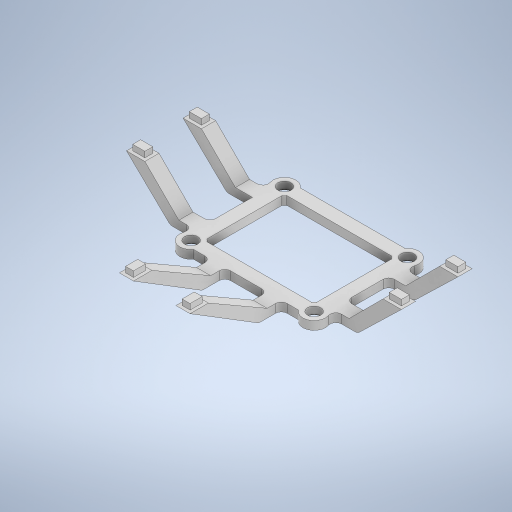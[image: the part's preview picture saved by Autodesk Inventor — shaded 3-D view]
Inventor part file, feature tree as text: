
AUTODESK INVENTOR PART (.ipt)
format: ipt  version: 2024.2 (Build 282272000, 272)  size: 465,920 bytes
history: native  units: mm
features: extrude x5, mirror x5, sketch x5, plane x4, fillet x2, chamfer x1
ambient origin geometry x8: Origin, YZ Plane, XZ Plane, XY Plane, X Axis, Y Axis, Z Axis, Center Point
bodies: Solid1 (feature_tree)
feature tree (22):
  extrude  "Extrusion1"  Depth=8.0mm
  chamfer  "Chamfer1"  Distance=4.7mm
  plane  "Work Plane2"
  extrude  "Extrusion2"  Depth=8.0mm
  plane  "Work Plane4"
  plane  "Work Plane5"
  mirror  "Mirror1"
  mirror  "Mirror2"
  plane  "Work Plane6"
  extrude  "Extrusion5"  Depth=4.0mm
  mirror  "Mirror5"
  extrude  "Extrusion4"  Depth=4.0mm
  mirror  "Mirror3"
  mirror  "Mirror4"
  extrude  "Extrusion6"  Depth=4.0mm
  fillet  "Fillet1"  Radius=4.0mm
  fillet  "Fillet2"  Radius=4.0mm
  sketch  "Sketch1"  dims[d0=4.7mm d1=8.0mm]
  sketch  "Sketch2"  dims[d2=4.7mm]
  sketch  "Sketch5"  dims[d3=8.0mm]
  sketch  "Sketch7"  dims[d4=4.7mm]
  sketch  "Sketch8"  dims[d5=8.0mm d6=4.7mm d7=8.0mm d8=4.0mm d9=4.0mm d10=4.0mm d11=4.0mm d12=4.0mm d13=4.0mm d14=4.0mm d15=4.0mm d16=33.0mm d17=4.7mm d18=4.7mm d19=4.7mm d20=4.7mm d21=2.35mm d22=2.35mm d23=2.35mm d24=2.35mm d25=43.5mm d26=3.0mm d27=0.0mm d28=0.5mm d29=2.0mm d30=45.0deg d32=4.0mm d41=5.0mm d42=0.0mm d47=21.75mm d48=16.5mm d49=6.5mm d61=9.0mm d62=4.3mm d63=2.8mm d64=1.1mm d65=1.1mm d66=2.0mm d67=0.0mm d71=9.25mm d72=8.0mm d73=6.5mm d76=5.0mm d77=0.0mm d78=2.8mm d79=4.3mm d80=2.8mm d81=4.3mm d82=1.1mm d83=1.1mm d84=1.1mm d85=1.1mm d86=2.0mm d87=0.0mm d91=6.0mm d93=45.0deg d94=15.0mm d95=15.0mm d96=2.0mm d97=2.0mm d98=5.0mm d99=30.0deg]
